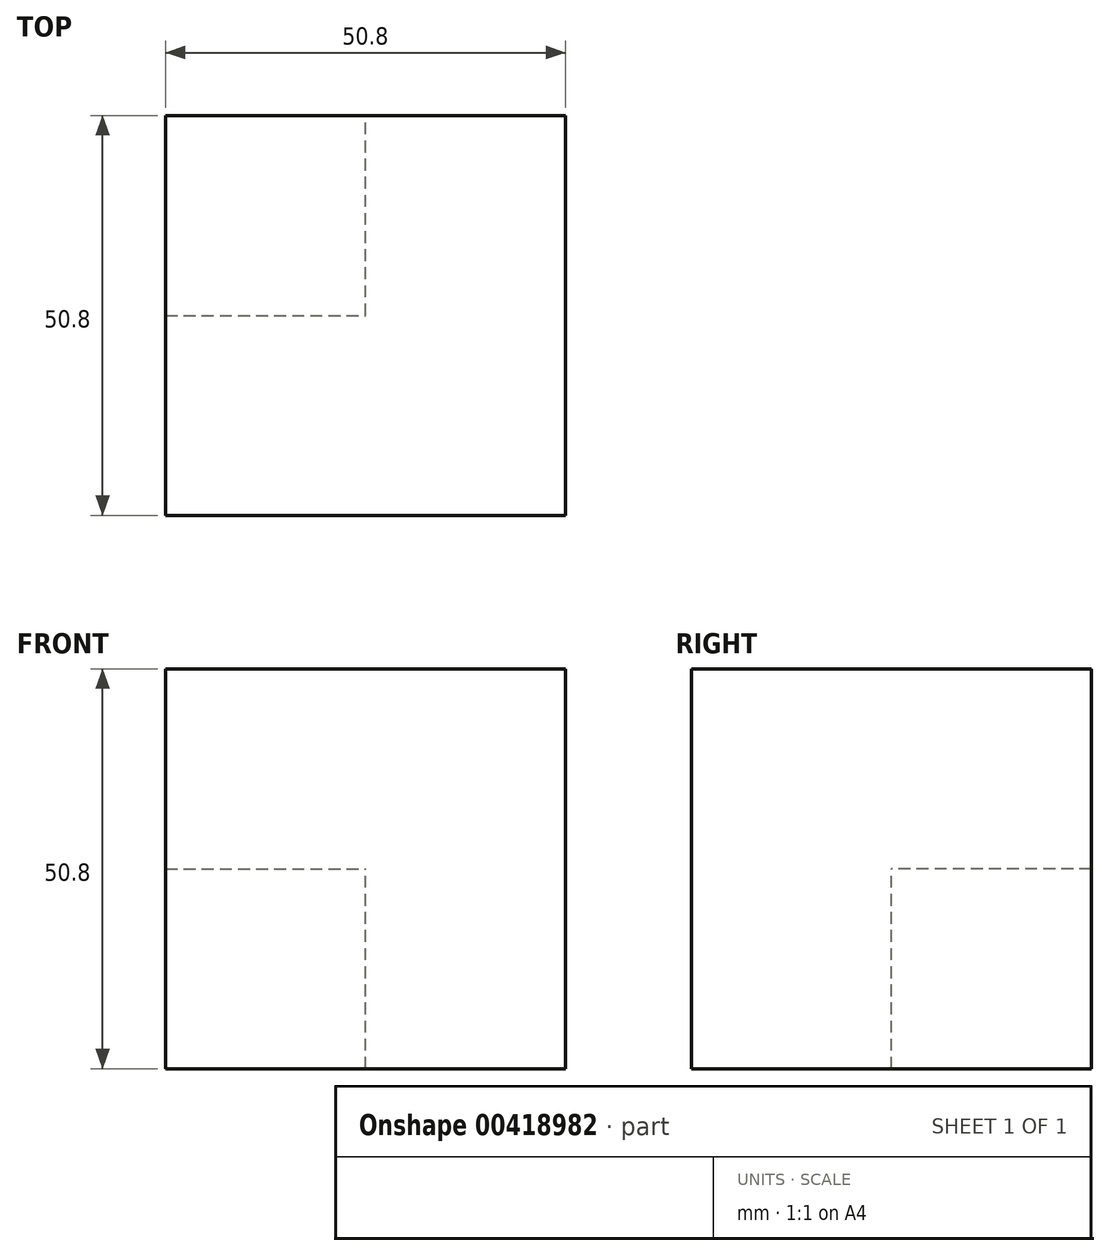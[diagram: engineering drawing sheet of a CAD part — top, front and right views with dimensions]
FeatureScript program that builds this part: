
annotation { "Feature Type Name" : "Feature", "Feature Type Description" : "" }
export const myFeature = defineFeature(function(context is Context, id is Id, definition is map)
    precondition{}
    {
        {
            var Q0;
            Q0=qCreatedBy(makeId("Front.planeOp"),FACE);
            var sketch = newSketch(context, id + "F0", { "sketchPlane" : qUnion([Q0])});
            skLineSegment(sketch, "E0.bottom", {"start": v(0, 0) * mm, "end": v(-25.4, 0) * mm});
            skLineSegment(sketch, "E0.top", {"start": v(0, 50.8) * mm, "end": v(-25.4, 50.8) * mm});
            skLineSegment(sketch, "E0.left", {"start": v(0, 0) * mm, "end": v(0, 50.8) * mm});
            skLineSegment(sketch, "E0.right", {"start": v(-25.4, 0) * mm, "end": v(-25.4, 50.8) * mm});
            skSolve(sketch);
        }
        {
            var Q0;
            Q0=makeQuery(id+"F0.imprint","IMPRINT",FACE,{"disambiguationData":[TD([[makeQuery(id+"F0.imprint","IMPRINT",EDGE,{"derivedFrom":sQuery(id+"F0.wireOp",EDGE,"E0.bottom")}),-1.0]])]});
            extrude(context, id + "F1", {"entities" : qUnion([Q0]), "depth" : 50.8 * mm});
        }
        {
            var Q0;
            Q0=makeQuery(id+"F1.opExtrude","SWEPT_FACE",FACE,{"disambiguationData":[OSD([sQuery(id+"F0.wireOp",EDGE,"E0.right")])]});
            var sketch = newSketch(context, id + "F2", { "sketchPlane" : qUnion([Q0])});
            skLineSegment(sketch, "E1.bottom", {"start": v(0, 0) * mm, "end": v(25.4, 0) * mm});
            skLineSegment(sketch, "E1.top", {"start": v(0, 25.4) * mm, "end": v(25.4, 25.4) * mm});
            skLineSegment(sketch, "E1.left", {"start": v(0, 0) * mm, "end": v(0, 25.4) * mm});
            skLineSegment(sketch, "E1.right", {"start": v(25.4, 0) * mm, "end": v(25.4, 25.4) * mm});
            skSolve(sketch);
        }
        {
            var Q0;
            {var subQ5=sQuery(id+"F2.wireOp",EDGE,"E1.top");Q0=makeQuery(id+"F2.imprint","IMPRINT",FACE,{"disambiguationData":[TD([[makeQuery(id+"F2.imprint","IMPRINT",EDGE,{"derivedFrom":subQ5}),1.0]])]});}
            extrude(context, id + "F3", {"entities" : qUnion([Q0]), "operationType" : NewBodyOperationType.ADD, "depth" : 25.4 * mm});
        }
    });
